# Revit family: Trim-Handle-Waterworks-Flyte-Thermostatic_Controlq
name_source: partatom
category: Plumbing Fixtures
revit_build: Autodesk Revit MEP 2014 (Build: 20140709_2115(x64)
units: mm (PartAtom-declared; Revit-internal decimal feet)

## types (1)
- NOT A TYPE - Load Type Catalog
    ADA Compliant = Yes
    Anti-scald Protection = No
    Assembly Code = D2010
    CW Connection = Yes
    CWFU = 0
    Certification IAPMO = Yes
    Certification State of MA = Yes
    Certification cUPC = Yes
    Code Compliance = Code # FLSV10: Complies with ASME A112.18.1/CSA B125.1, ASTM E 1621-05, ANSI A117.1 ADA. Certified with IAPMO, cUPC & State of MA
    Constraint = 1
    Control Valve Rough-in Depth Maximum = 0' - 4 1/4"
    Control Valve Rough-in Depth Minimum = 0' - 3 1/4"
    ControlM = 1
    Cross Handles = No
    Default Elevation = 2' - 10"
    Depth = 0' - 2 5/8"
    Description = Flyte Thermostatic Control Valve Trim with Metal Lever Handle in Chrome
    Diverter Valve Rough-in Depth Maximum = 0' - 4 1/4"
    Diverter Valve Rough-in Depth Minimum = 0' - 3 1/4"
    Finish = Metal - Waterworks - Chrome
    Fittings Hole Diameter = 0' - 4 1/2"
    HW Connection = Yes
    HWFU = 0
    Height = 0' - 5 1/2"
    Hot Limit Safety Stop = No
    Keynote = 22 40 00
    Length = 0' - 5 1/2"
    Lever Handles = Yes
    Manufacturer = Waterworks
    Model = FLTH10
    Model SKU = 05-78610-04662
    Product Documentation Link = http://assets.waterworks.com
    Product Name = Flyte Thermostatic Control Valve Trim with Metal Lever Handle
    Product Page URL = http://www.waterworks.com
    URL = http://www.waterworks.com
    Vent Connection = No
    Version = 2014 - v1.0a
    WFU = 0
    Warranty = http://www.waterworks.com
    Waste Connection = No
    ‌Installation Requirements or Notes = Requires 1/2'' valve rough GUTH56 (USA) or GU56TH (UK) sold separately

## geometry (parser evidence)
native form markers: Sweep x3
no freeform markers — native parametric forms only
